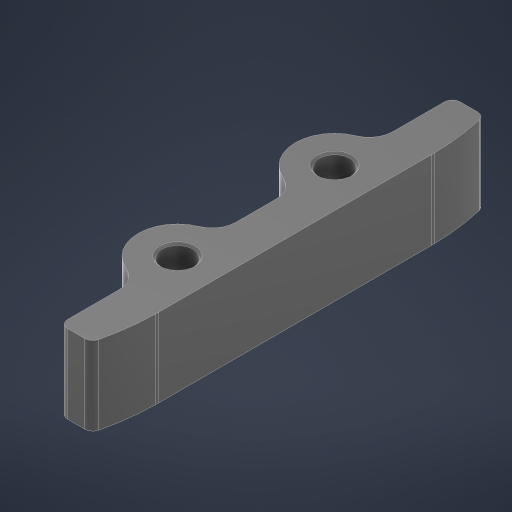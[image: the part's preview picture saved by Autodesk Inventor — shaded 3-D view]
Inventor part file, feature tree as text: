
AUTODESK INVENTOR PART (.ipt)
format: ipt  version: 2024 (Build 280153000, 153)  size: 233,984 bytes
history: native  units: mm
features: fillet x3, extrude x1, chamfer x1, sketch x1
ambient origin geometry x8: Origin, YZ Plane, XZ Plane, XY Plane, X Axis, Y Axis, Z Axis, Center Point
bodies: Solid1 (feature_tree)
feature tree (6):
  extrude  "Extrusion1"  Depth=20.0mm
  fillet  "Fillet1"  Radius=4.0mm
  fillet  "Fillet2"  Radius=10.0mm
  fillet  "Fillet3"  Radius=10.0mm
  chamfer  "Chamfer1"  Distance=5.0mm
  sketch  "Sketch1"  dims[d0=4.0mm d1=20.0mm d2=4.0mm d3=10.0mm d4=10.0mm d5=5.0mm d6=25.0mm d7=25.0mm d8=10.0mm d9=4.0mm d10=10.0mm d11=4.0mm d12=17.5mm d13=17.5mm d14=30.0mm d15=30.0mm d16=10.0mm d17=0.0mm d18=3.0mm d19=1.0mm d20=25.0mm d21=0.25mm d22=2.0mm d23=45.0deg]
